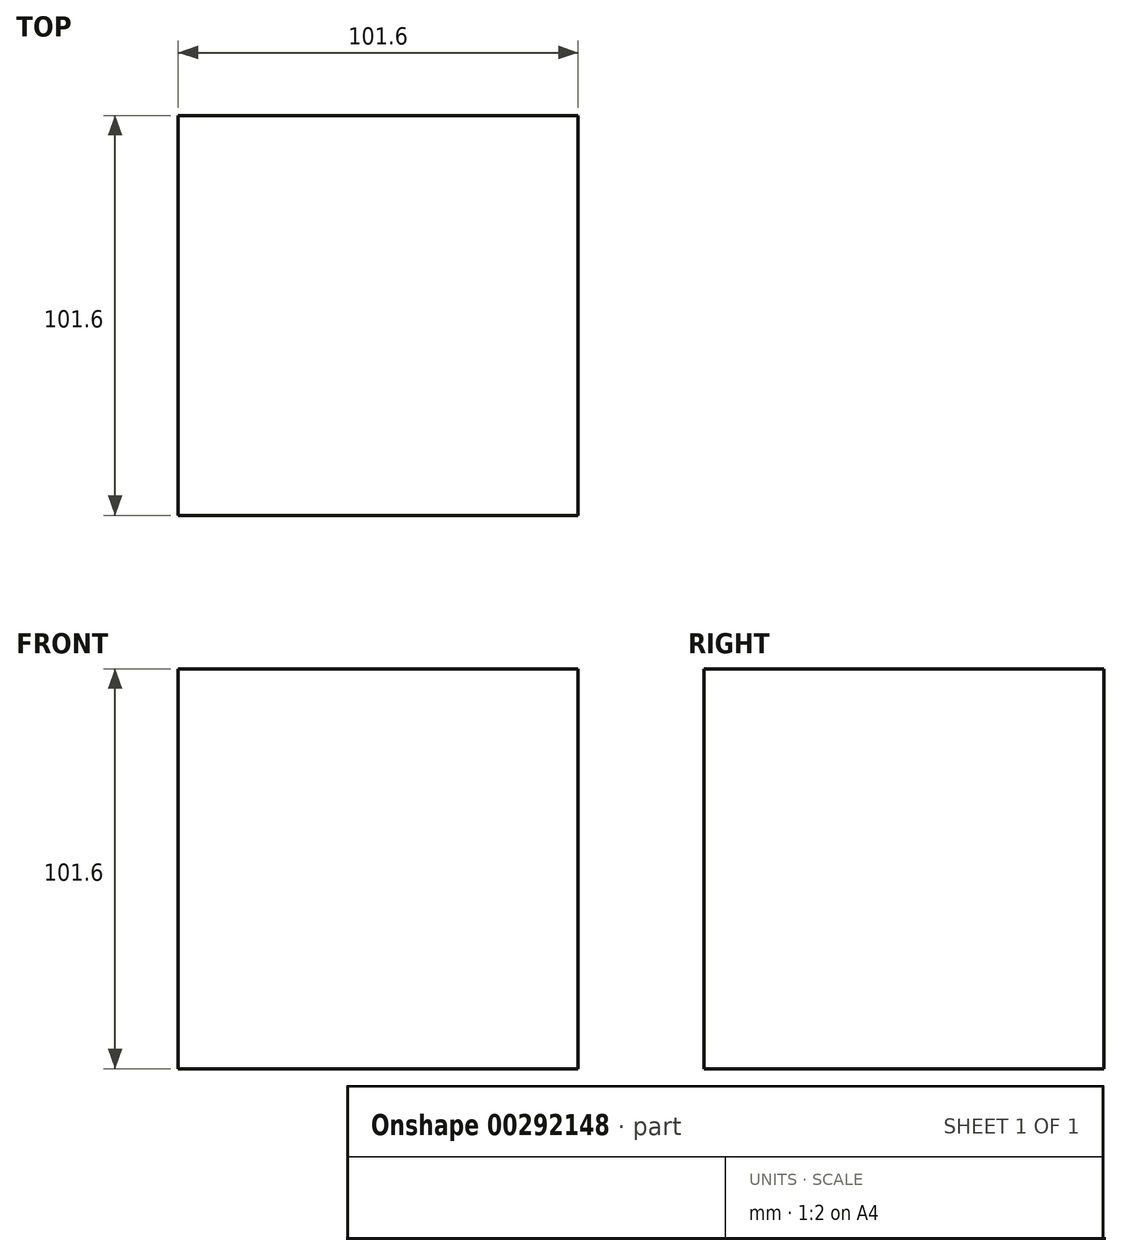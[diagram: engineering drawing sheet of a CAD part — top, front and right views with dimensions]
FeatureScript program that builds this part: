
annotation { "Feature Type Name" : "Feature", "Feature Type Description" : "" }
export const myFeature = defineFeature(function(context is Context, id is Id, definition is map)
    precondition{}
    {
        {
            var Q0;
            Q0=qCreatedBy(makeId("Front.planeOp"),FACE);
            var sketch = newSketch(context, id + "F0", { "sketchPlane" : qUnion([Q0])});
            skLineSegment(sketch, "E0.bottom", {"start": v(-50.8, 50.8) * mm, "end": v(50.8, 50.8) * mm});
            skLineSegment(sketch, "E0.top", {"start": v(-50.8, -50.8) * mm, "end": v(50.8, -50.8) * mm});
            skLineSegment(sketch, "E0.left", {"start": v(-50.8, 50.8) * mm, "end": v(-50.8, -50.8) * mm});
            skLineSegment(sketch, "E0.right", {"start": v(50.8, 50.8) * mm, "end": v(50.8, -50.8) * mm});
            skPoint(sketch, "E0.middle", {"position": v(0, 0) * mm});
            skSolve(sketch);
        }
        {
            var Q0;
            Q0 = qSketchRegion(id + "F0", true);
            extrude(context, id + "F1", {"entities" : qUnion([Q0]), "depth" : 101.6 * mm});
        }
    });
